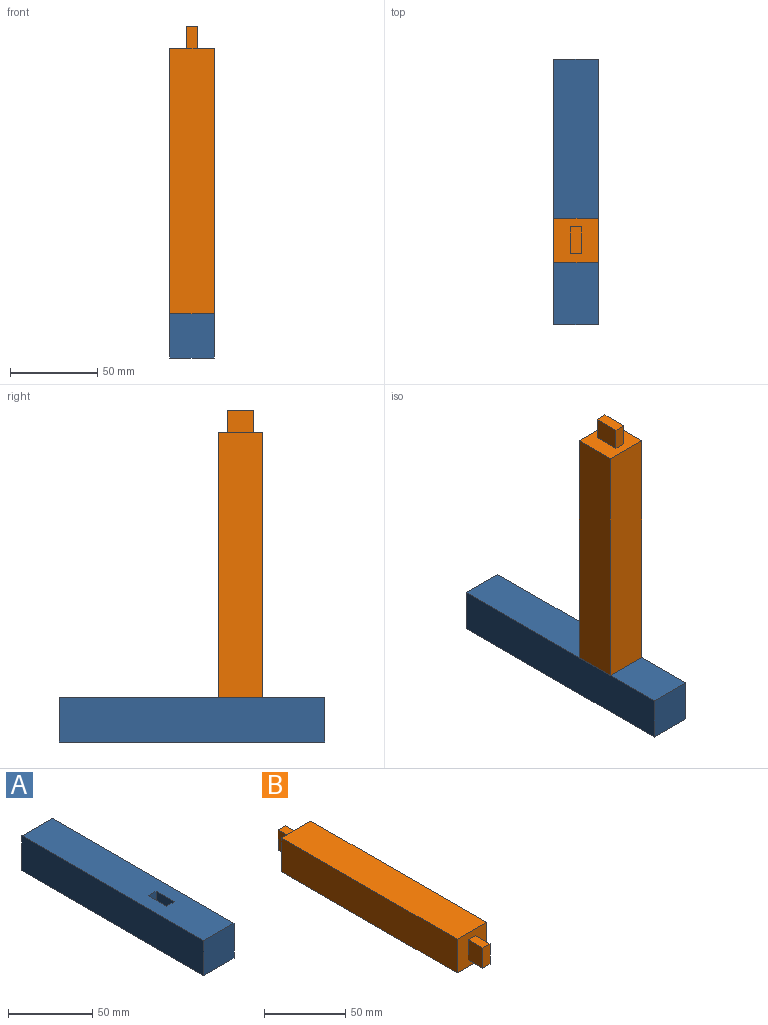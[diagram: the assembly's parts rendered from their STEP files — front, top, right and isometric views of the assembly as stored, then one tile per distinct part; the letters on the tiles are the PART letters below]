
ASSEMBLY  parts=2 mates=1
PART A: 11 faces, bbox 25.4x152.4x25.4 mm
  f0: plane 152.4x25.4mm, normal (0,0,1), area 3774.2mm2, adj f2,f3,f4,f5,f6,f7,f8,f9
  f1: plane 152.4x25.4mm, normal (0,0,-1), area 3871mm2, adj f2,f3,f4,f5
  f2: plane 152.4x25.4mm, normal (1,0,0), area 3871mm2, adj f0,f1,f4,f5
  f3: plane 152.4x25.4mm, normal (-1,0,0), area 3871mm2, adj f0,f1,f4,f5
  f4: plane 25.4x25.4mm, normal (0,-1,0), area 645.2mm2, adj f0,f1,f2,f3
  f5: plane 25.4x25.4mm, normal (0,1,0), area 645.2mm2, adj f0,f1,f2,f3
  f6: plane 12.7x6.35mm, normal (0,1,0), area 80.6mm2, adj f0,f7,f9,f10
  f7: plane 15.24x12.7mm, normal (-1,0,0), area 193.5mm2, adj f0,f6,f8,f10
  f8: plane 12.7x6.35mm, normal (0,-1,0), area 80.6mm2, adj f0,f7,f9,f10
  f9: plane 15.24x12.7mm, normal (1,0,0), area 193.5mm2, adj f0,f6,f8,f10
  f10: plane 15.24x6.35mm, normal (0,0,1), area 96.8mm2, adj f6,f7,f8,f9
PART B: 16 faces, bbox 25.4x177.8x25.4 mm
  f0: plane 25.4x25.4mm, normal (0,-1,0), area 548.4mm2, adj f1,f2,f3,f4,f6,f7,f8,f9
  f1: plane 152.4x25.4mm, normal (0,0,-1), area 3871mm2, adj f0,f2,f4,f5
  f2: plane 152.4x25.4mm, normal (1,0,0), area 3871mm2, adj f0,f1,f3,f5
  f3: plane 152.4x25.4mm, normal (0,0,1), area 3871mm2, adj f0,f2,f4,f5
  f4: plane 152.4x25.4mm, normal (-1,0,0), area 3871mm2, adj f0,f1,f3,f5
  f5: plane 25.4x25.4mm, normal (0,1,0), area 548.4mm2, adj f1,f2,f3,f4,f11,f12,f13,f14
  f6: plane 12.7x6.35mm, normal (0,0,-1), area 80.6mm2, adj f0,f7,f9,f10
  f7: plane 15.24x12.7mm, normal (1,0,0), area 193.5mm2, adj f0,f6,f8,f10
  f8: plane 12.7x6.35mm, normal (0,0,1), area 80.6mm2, adj f0,f7,f9,f10
  f9: plane 15.24x12.7mm, normal (-1,0,0), area 193.5mm2, adj f0,f6,f8,f10
  f10: plane 15.24x6.35mm, normal (0,-1,0), area 96.8mm2, adj f6,f7,f8,f9
  f11: plane 12.7x6.35mm, normal (0,0,-1), area 80.6mm2, adj f5,f12,f14,f15
  f12: plane 15.24x12.7mm, normal (-1,0,0), area 193.5mm2, adj f5,f11,f13,f15
  f13: plane 12.7x6.35mm, normal (0,0,1), area 80.6mm2, adj f5,f12,f14,f15
  f14: plane 15.24x12.7mm, normal (1,0,0), area 193.5mm2, adj f5,f11,f13,f15
  f15: plane 15.24x6.35mm, normal (0,1,0), area 96.8mm2, adj f11,f12,f13,f14
PLACE A t=(-16.8,-4.14,8.34)mm fixed
PLACE B rot(axis=(1,0,0),90deg) t=(-16.8,-108.28,173.44)mm
MATE fastened A.f10 <-> B.f10  axis (0,0,1) through (-16.8,-108.28,8.34)mm
